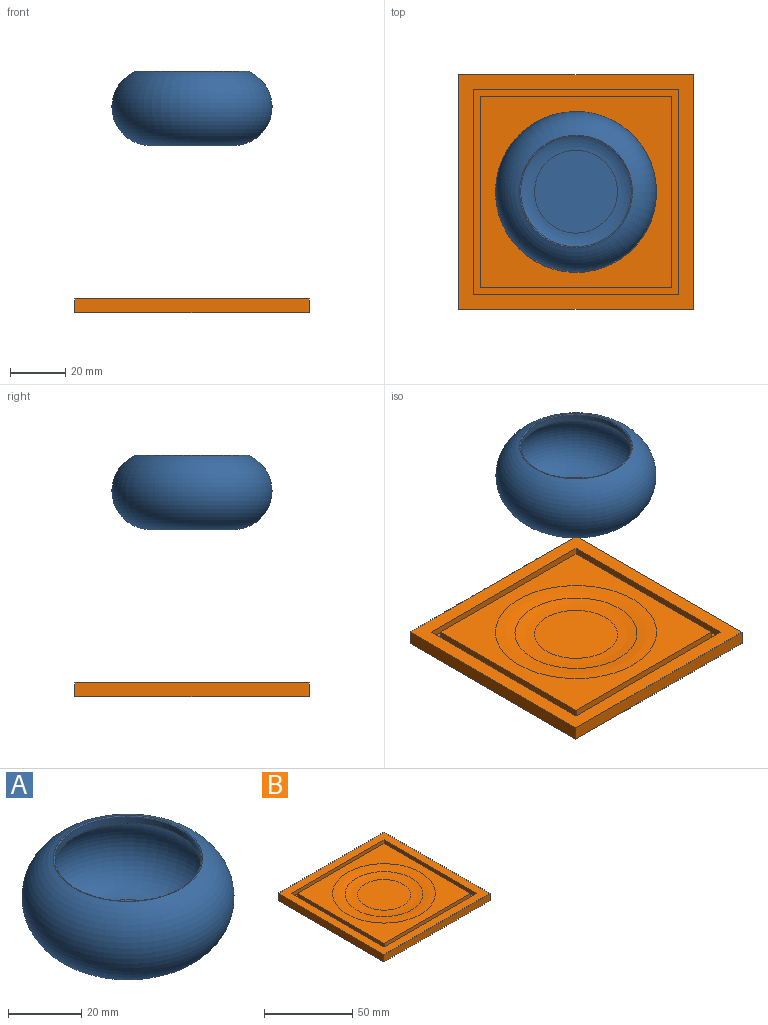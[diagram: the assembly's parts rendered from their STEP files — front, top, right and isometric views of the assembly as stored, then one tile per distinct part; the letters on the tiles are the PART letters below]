
ASSEMBLY  parts=2 mates=1
PART A: 7 faces, bbox 62.8x62.8x28 mm
  f0: torus R=15mm, axis (0,0,1), area 5988.2mm2, adj f1,f5
  f1: plane 30x30mm, normal (0,0,-1), area 706.9mm2, adj f0
  f2: cylinder r=20mm len=40mm, axis (0,0,1), area 262.7mm2, adj f5,f6
  f3: plane 30x30mm, normal (0,0,1), area 706.9mm2, adj f4
  f4: torus R=15mm, axis (0,0,1), area 4473.5mm2, adj f3,f6
  f5: torus R=20.3mm, axis (0,0,-1), area 74.8mm2, adj f0,f2
  f6: torus R=20.3mm, axis (0,0,-1), area 41.8mm2, adj f2,f4
PART B: 19 faces, bbox 85x85x5 mm
  f0: plane 85x85mm, normal (0,0,1), area 1714.2mm2, adj f1,f2,f3,f4,f9,f10,f11,f12
  f1: plane 85x5mm, normal (0,1,0), area 425mm2, adj f0,f2,f4,f5
  f2: plane 85x5mm, normal (-1,0,0), area 425mm2, adj f0,f1,f3,f5
  f3: plane 85x5mm, normal (0,-1,0), area 425mm2, adj f0,f2,f4,f5
  f4: plane 85x5mm, normal (1,0,0), area 425mm2, adj f0,f1,f3,f5
  f5: plane 85x85mm, normal (0,0,-1), area 7225mm2, adj f1,f2,f3,f4
  f6: plane 69.23x2.5mm, normal (-1,0,0), area 173.1mm2, adj f7,f13,f14,f15
  f7: plane 69.23x2.5mm, normal (0,1,0), area 173.1mm2, adj f6,f8,f14,f15
  f8: plane 69.23x2.5mm, normal (1,0,0), area 173.1mm2, adj f7,f13,f14,f15
  f9: plane 74.23x2.5mm, normal (-1,0,0), area 185.6mm2, adj f0,f10,f12,f14
  f10: plane 74.23x2.5mm, normal (0,-1,0), area 185.6mm2, adj f0,f9,f11,f14
  f11: plane 74.23x2.5mm, normal (1,0,0), area 185.6mm2, adj f0,f10,f12,f14
  f12: plane 74.23x2.5mm, normal (0,1,0), area 185.6mm2, adj f0,f9,f11,f14
  f13: plane 69.23x2.5mm, normal (0,-1,0), area 173.1mm2, adj f6,f8,f14,f15
  f14: plane 74.23x74.23mm, normal (0,0,1), area 717.3mm2, adj f6,f7,f8,f9,f10,f11,f12,f13
  f15: plane 69.23x69.23mm, normal (0,0,1), area 2122.7mm2, adj f6,f7,f8,f13,f18
  f16: plane 30.1x30.1mm, normal (0,0,1), area 711.6mm2, adj f17
  f17: torus R=15.05mm, axis (0,0,-1), area 826.3mm2, adj f16,f18
  f18: torus R=29.16mm, axis (0,0,1), area 1139.4mm2, adj f15,f17
PLACE A t=(0,0,60.53)mm
PLACE B at identity
MATE slider A.f0 <-> B.f17  axis (0,0,1) through (0,0,60.53)mm
